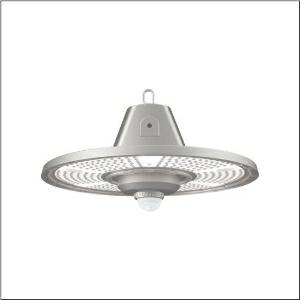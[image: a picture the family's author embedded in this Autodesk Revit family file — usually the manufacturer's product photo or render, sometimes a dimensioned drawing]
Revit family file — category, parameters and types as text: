
# Revit family: highbay_31-l_51hc427a4mmb01
name_source: partatom
category: Lighting Fixtures
units: mm (PartAtom-declared; Revit-internal decimal feet)

## family parameters
Cut with Voids When Loaded = No
Host = Face
Light Source = No
Part Type = Normal
Room Calculation Point = No
Round Connector Dimension = Use Diameter
Shared = No

## types (1)
- Highbay 31-L (1 x LED, 28000 lm, 187 W, 4000K)
    Apparent Load = 187 VA
    CIE Flux Codes = 83 98 100 100 100
    Color Rendering = 80
    Color Temperature = 4000K
    Default Elevation = 1800 mm
    Description = Highbay 31-L, high bay luminaire, primary light control with lens, of PC, primary optical cover: cover panel, of PC, transparent, light emission: direct distribution, primary light characteristic: rotationally symmetric, installation type: suspended mounting, surface-mounted, LED, rated luminous flux: 28.000lm, luminous efficacy: 150lm/W, light colour: 840, colour temperature: 4000K, control gear: ON/OFF, with cable, 3x 1.0mm², free wire ends, mains connection: 220..240V, AC/DC, 0/50..60Hz, cable length: 1,5m, rated input power: 187W, housing, rotationally symmetric, of diecast aluminium, powder-coated, grey aluminium (RAL 9007), with hook on luminaire side, incl. screw, diameter: 406mm, PIR sensor, protection rating (complete): IP65, insulation class (complete): insulation class I (protective earthing), certification: CE, ENEC, UKCA, protection symbol: D, impact resistance: IK08, permissible operating ambient temperature: -30..+45°C, standard: EN 60598-2-22, EN 60598, corresponds to IFS (International Featured Standards) requirements for safety and quality in the food industry, packaging unit: 1 piece
    Height = 160 mm
    Lamp = 1 x LED
    Lamp Light Flux = 28000 lm
    Lamp Power = 187 W
    Lamp count = 1
    Length = 406 mm
    Luminous efficacy = 150 lm/W
    Manufacturer = Siteco
    ModVariant = No
    Model = 51HC427A4MMB01
    Mounting Place = Ceiling
    Mounting Type = Pendant
    Number of Poles = 1
    OnlyDefault = Yes
    Power Factor = 1
    Product Name = Highbay 31-L
    Product group = high bay luminaire
    ProductGroupID = 901
    Protection Class = Protection class I
    Protection Degree = IP 65
    RLX_Detail_Level = 1
    RLX_Emergency_Light_Flux = 0 lm
    RLX_Emergency_Type = 0
    RLX_Emergency_Type_DB = No
    RlxData = <blob elided: 121057 chars, md5=8ee9c998>
    Socket = socket
    Standby Power = 0 W
    System Light Flux = 28000 lm
    System Power = 187 W
    Type Comments = Product without accessories
    Type Image = l_384981.jpg
    URL = http://relux.com
    VarID = ---
    Voltage = 0 V
    Weight = 0.00 kg
    Width = 0 mm  [stored 0 ft]

note: [stored X ft] marks values corroborated as IEEE doubles in the binary element streams (Revit-internal decimal feet)

## geometry (parser evidence)
native form markers: Blend x4, Sweep x11
no freeform markers — native parametric forms only
